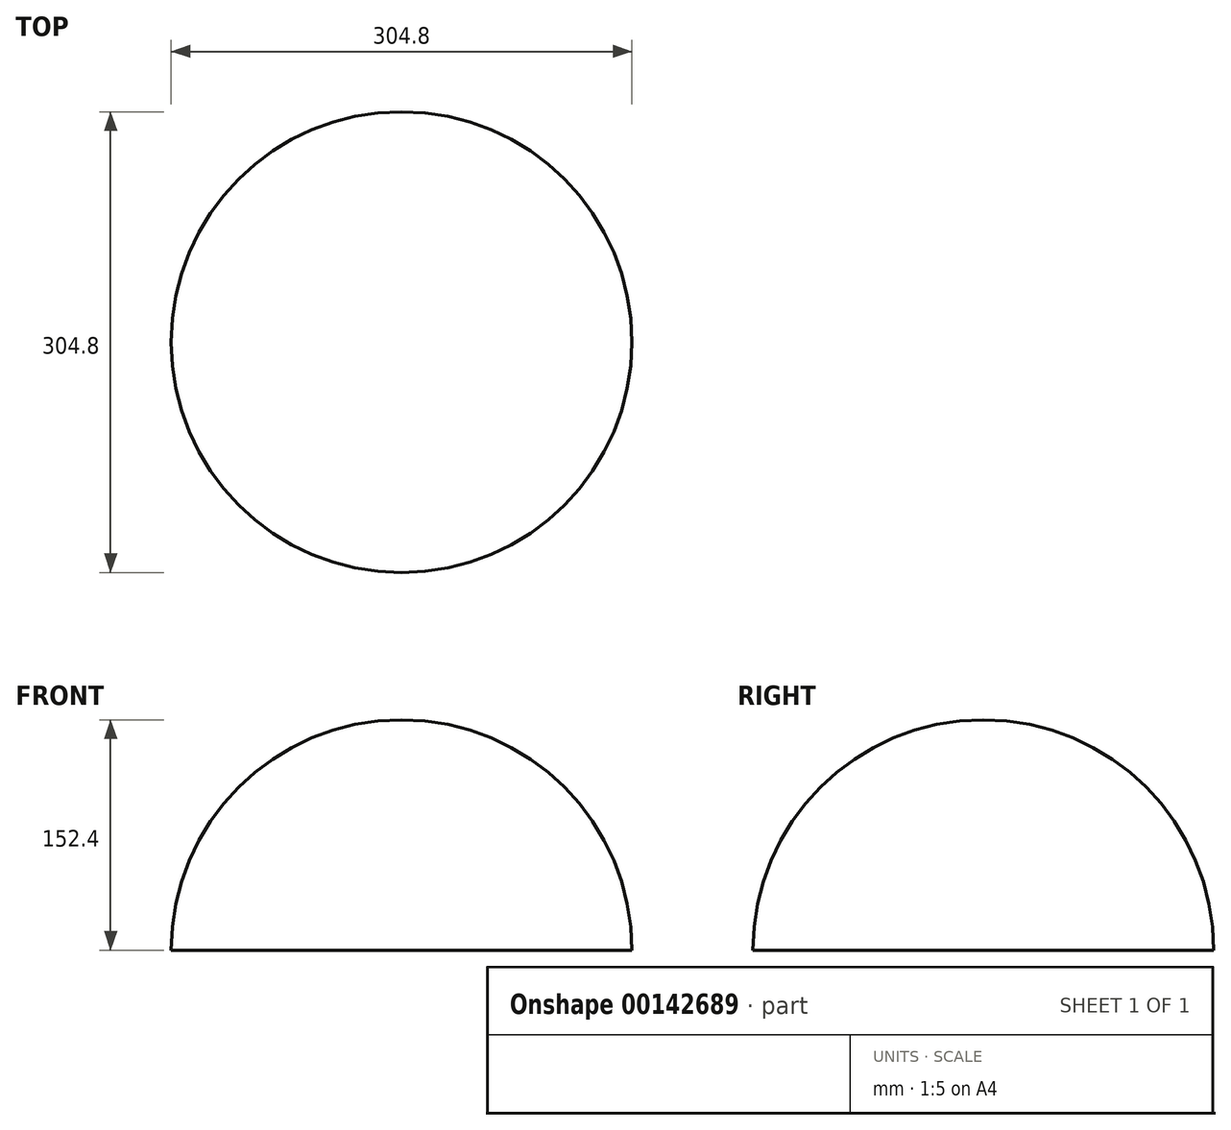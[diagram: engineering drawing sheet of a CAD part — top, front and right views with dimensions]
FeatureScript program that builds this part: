
annotation { "Feature Type Name" : "Feature", "Feature Type Description" : "" }
export const myFeature = defineFeature(function(context is Context, id is Id, definition is map)
    precondition{}
    {
        {
            var Q0;
            Q0=qCreatedBy(makeId("Top.planeOp"),FACE);
            var sketch = newSketch(context, id + "F0", { "sketchPlane" : qUnion([Q0])});
            skArc(sketch, "E0", {"start": v(0, -152.4) * mm, "mid": v(152.4, 0) * mm, "end": v(0, 152.4) * mm});
            skLineSegment(sketch, "E1", {"start": v(0, -152.4) * mm, "end": v(0, 152.4) * mm});
            skSolve(sketch);
        }
        {
            var Q0;
            Q0=makeQuery(id+"F0.imprint","IMPRINT",FACE,{"disambiguationData":[TD([[makeQuery(id+"F0.imprint","IMPRINT",EDGE,{"derivedFrom":sQuery(id+"F0.wireOp",EDGE,"E0")}),1.0]])]});
            var Q1;
            Q1=sQuery(id+"F0.wireOp",EDGE,"E1");
            revolve(context, id + "F1", {"entities" : qUnion([Q0]), "axis" : qUnion([Q1]), "revolveType" : RevolveType.ONE_DIRECTION, "oppositeDirection" : true, "angle" : 180 * degree});
        }
    });
